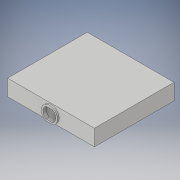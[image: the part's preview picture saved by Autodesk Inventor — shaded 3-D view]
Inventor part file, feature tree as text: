
AUTODESK INVENTOR PART (.ipt)
format: ipt  version: 2017 (Build 210142000, 142)  size: 333,824 bytes
history: native  units: in
note: dims shown in document units (in); Inventor stores cm internally (conversion verified against a paired STEP export)
features: extrude x7, sketch x6
ambient origin geometry x8: Origin, YZ Plane, XZ Plane, XY Plane, X Axis, Y Axis, Z Axis, Center Point
bodies: Solid1 (feature_tree), Solid2 (feature_tree)
feature tree (13):
  extrude  "cubicals"  Depth=12.0in
  extrude  "floor"  Depth=2.5in
  extrude  "walls"  Depth=0.0833in
  sketch  "Sketch4"  dims[d10=0.0833in d95=0.0833in]
  extrude  "connection"  Depth=0.0833in
  extrude  "light connection"  Depth=2.5in
  extrude  "connection cut"  Depth=2.5in
  extrude  "ceiling"  Depth=1.0in
  sketch  "Sketch2"  dims[d2=4.5in d3=0.0in d4=12.0in]
  sketch  "Sketch3"  dims[d5=8.0in d7=2.5in]
  sketch  "Sketch5"  dims[d97=0.0833in d98=0.0833in]
  sketch  "Sketch6"  dims[d99=12.0in d100=8.0in d102=0.0833in d103=0.0833in d104=0.0833in d105=0.0833in]
  sketch  "Sketch7"  dims[d106=12.0in d107=8.0in d109=0.0833in d110=0.0833in d111=0.0833in d112=0.0833in d113=2.5in d114=2.5in d115=3.0in d117=3.0in d118=6.0in d120=6.0in d121=1.0in d122=0.0in d128=1.0in d129=1.0in d130=1.0in d131=1.0in d132=1.0in d133=1.0in d134=7.7746in d135=0.0in d148=4.0in d149=1.0in d150=4.8944in d151=0.5833in d152=3.8873in d153=3.8873in d154=1.7083in d155=0.0625in d156=0.0625in d157=1.6458in d158=0.125in d159=0.125in d160=1.0in d161=0.0in d164=0.25in d165=0.125in d166=45.0deg d167=0.0892in d168=0.0884in d169=1.0in d170=0.0in d171=1.0in d172=0.0in d173=1.0in d174=0.0in]
